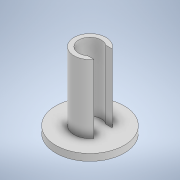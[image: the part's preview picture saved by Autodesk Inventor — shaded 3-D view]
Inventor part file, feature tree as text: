
AUTODESK INVENTOR PART (.ipt)
format: ipt  version: 2022 (Build 260153000, 153)  size: 115,200 bytes
history: native  units: in
note: dims shown in document units (in); Inventor stores cm internally (conversion verified against a paired STEP export)
features: sketch x3, extrude x2
ambient origin geometry x8: Origin, YZ Plane, XZ Plane, XY Plane, X Axis, Y Axis, Z Axis, Center Point
bodies: Solid1 (feature_tree)
feature tree (5):
  sketch  "Sketch1"  dims[d0=0.3937in d1=0.5512in]
  extrude  "Extrusion1"  Depth=0.3937in
  extrude  "Extrusion2"  Depth=0.315in
  sketch  "Sketch2"  dims[d2=0.3937in d3=0.315in]
  sketch  "Sketch3"  dims[d4=0.1181in d5=1.1811in d6=0.0in d7=1.1811in d8=0.1181in d9=0.0in]
